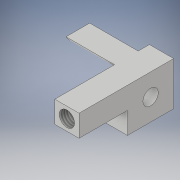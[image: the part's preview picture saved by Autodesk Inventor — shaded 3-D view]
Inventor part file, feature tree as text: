
AUTODESK INVENTOR PART (.ipt)
format: ipt  version: 2019 (Build 230136000, 136)  size: 146,944 bytes
history: native  units: in
note: dims shown in document units (in); Inventor stores cm internally (conversion verified against a paired STEP export)
features: sketch x5, extrude x4, hole x1, thread x1
ambient origin geometry x8: Origin, YZ Plane, XZ Plane, XY Plane, X Axis, Y Axis, Z Axis, Center Point
bodies: Solid1 (feature_tree)
feature tree (11):
  sketch  "Sketch1"  dims[d0=0.4488in d1=0.4764in]
  extrude  "Extrusion1"  Depth=0.4764in
  extrude  "Extrusion2"  Depth=0.1162in
  sketch  "Sketch3"  dims[d2=0.244in d3=0.1162in]
  sketch  "Sketch6"  dims[d4=0.25in d5=0.0in d6=0.5in d7=0.0in]
  hole  "Hole2"  [1 undecoded]
  extrude  "Extrusion8"  Depth=0.4764in
  sketch  "Sketch7"  dims[d19=0.4764in d20=0.2382in]
  extrude  "Extrusion9"  Depth=0.4488in
  thread  "Thread2"  [1 undecoded]
  sketch  "Sketch8"  dims[d29=0.0787in d30=0.4488in d31=0.2244in d33=0.4488in d37=0.1575in d38=0.75in d39=0.119in d40=0.25in d41=0.5635in d42=1.0in d43=0.8108in d46=0.2244in d47=0.5in d48=0.0in d50=0.25in d51=0.2244in d52=0.1122in d53=0.125in d63=0.1122in d64=0.125in d65=0.1575in d66=0.35in d67=0.0in d68=1.0in d69=0.0in d54=1.0in d55=1.0in d56=1.0in d57=0.15in d58=0.25in d59=0.375in d60=0.5635in d61=0.75in d62=0.8108in]
note: 2 required parameter values undecoded (feature->parameter linkage not recoverable at this tier; creation-order binding heuristic only, values carry confidence <= 0.55)
